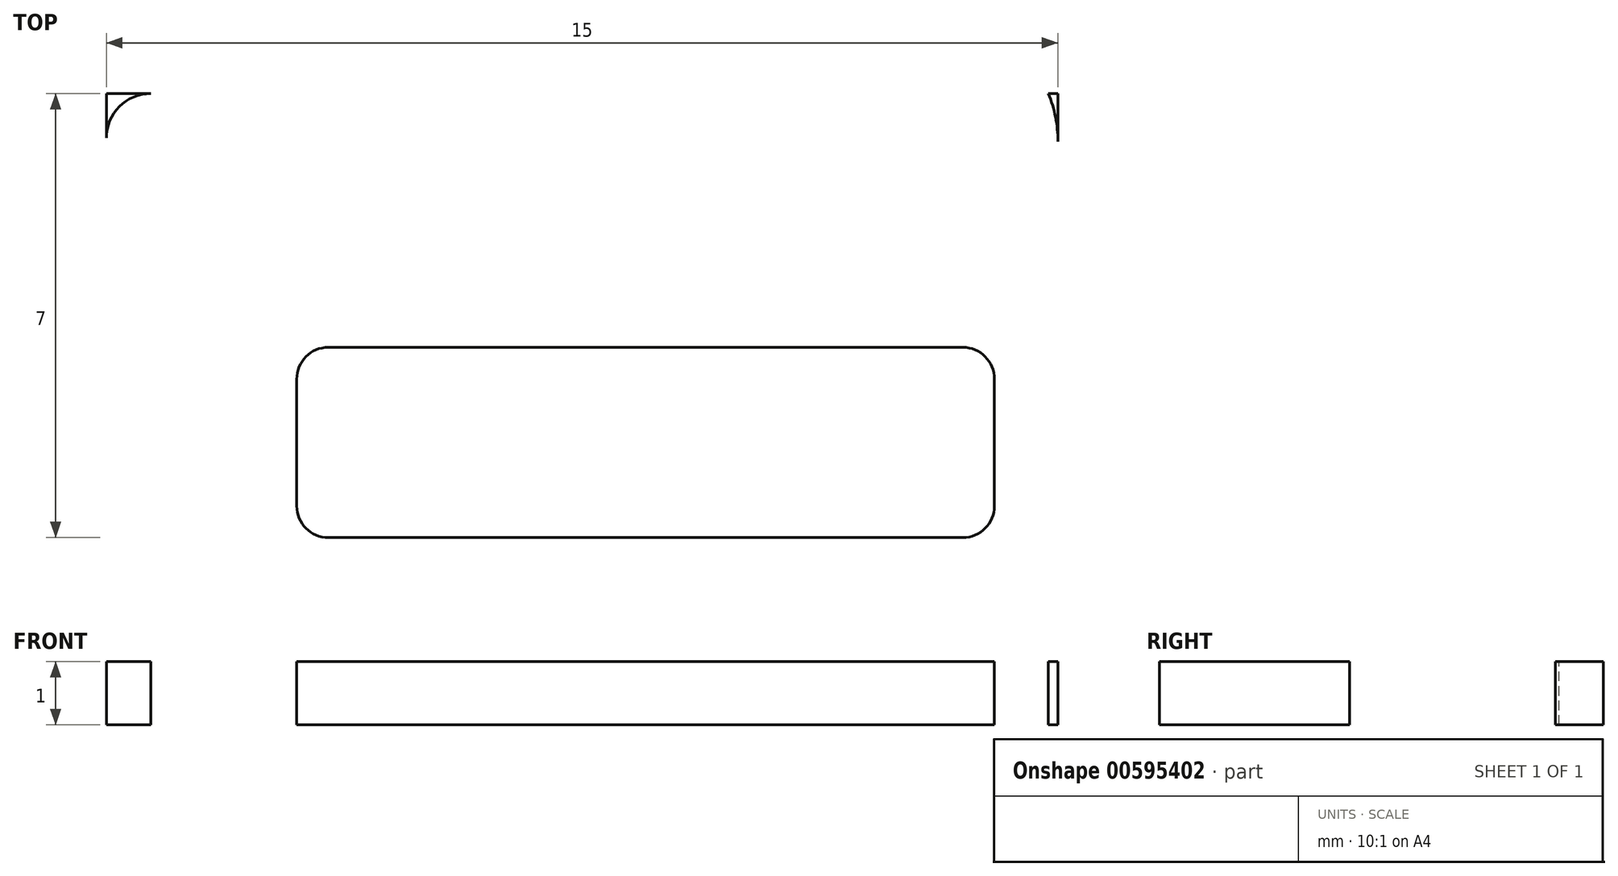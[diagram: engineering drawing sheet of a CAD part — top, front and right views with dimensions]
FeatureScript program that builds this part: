
annotation { "Feature Type Name" : "Feature", "Feature Type Description" : "" }
export const myFeature = defineFeature(function(context is Context, id is Id, definition is map)
    precondition{}
    {
        {
            var Q0;
            Q0=qCreatedBy(makeId("Top.planeOp"),FACE);
            var sketch = newSketch(context, id + "F0", { "sketchPlane" : qUnion([Q0])});
            skLineSegment(sketch, "E0.bottom", {"start": v(7.5, 4.95) * mm, "end": v(-7.5, 4.95) * mm});
            skLineSegment(sketch, "E0.top", {"start": v(7.5, -4.95) * mm, "end": v(-7.5, -4.95) * mm});
            skLineSegment(sketch, "E0.left", {"start": v(7.5, 4.95) * mm, "end": v(7.5, -4.95) * mm});
            skLineSegment(sketch, "E0.right", {"start": v(-7.5, 4.95) * mm, "end": v(-7.5, -4.95) * mm});
            skPoint(sketch, "E0.middle", {"position": v(0, 0) * mm});
            skSolve(sketch);
        }
        {
            var Q0;
            Q0 = qSketchRegion(id + "F0", true);
            extrude(context, id + "F1", {"entities" : qUnion([Q0]), "depth" : 1 * mm, "offsetDistance" : 25 * mm});
        }
        {
            var Q0;
            Q0=makeQuery(id+"F1.opExtrude","CAP_FACE",FACE,{"disambiguationData":[OSD([sQuery(id+"F0.wireOp",EDGE,"E0.bottom"),sQuery(id+"F0.wireOp",EDGE,"E0.top"),sQuery(id+"F0.wireOp",EDGE,"E0.left"),sQuery(id+"F0.wireOp",EDGE,"E0.right")])],"isStart":false});
            var sketch = newSketch(context, id + "F2", { "sketchPlane" : qUnion([Q0])});
            skLineSegment(sketch, "E1", {"start": v(-13.1, -4.82) * mm, "end": v(-1.33, -6.84) * mm});
            skLineSegment(sketch, "E2", {"start": v(-1.67, -6.8) * mm, "end": v(5.5, -6.8) * mm});
            skLineSegment(sketch, "E3", {"start": v(7.5, -4.8) * mm, "end": v(7.5, 4.2) * mm});
            skLineSegment(sketch, "E4", {"start": v(5.5, 6.2) * mm, "end": v(-1.61, 6.2) * mm});
            skLineSegment(sketch, "E5", {"start": v(145.29, 22.9) * mm, "end": v(-1.39, 6.2) * mm});
            skLineSegment(sketch, "E6", {"start": v(-4, 0.95) * mm, "end": v(6, 0.95) * mm});
            skLineSegment(sketch, "E7", {"start": v(6.5, 0.45) * mm, "end": v(6.5, -1.55) * mm});
            skLineSegment(sketch, "E8", {"start": v(6, -2.05) * mm, "end": v(-4, -2.05) * mm});
            skLineSegment(sketch, "E9", {"start": v(-4.5, -1.55) * mm, "end": v(-4.5, 0.45) * mm});
            skLineSegment(sketch, "E10", {"start": v(-4.5, -6.55) * mm, "end": v(-4.5, -8.55) * mm});
            skLineSegment(sketch, "E11", {"start": v(-4, -9.05) * mm, "end": v(6, -9.05) * mm});
            skLineSegment(sketch, "E12", {"start": v(6.5, -8.55) * mm, "end": v(6.5, -6.55) * mm});
            skLineSegment(sketch, "E13", {"start": v(6, -6.05) * mm, "end": v(-4, -6.05) * mm});
            skLineSegment(sketch, "E14", {"start": v(-4.5, -13.55) * mm, "end": v(-4.5, -15.55) * mm});
            skLineSegment(sketch, "E15", {"start": v(-4, -16.05) * mm, "end": v(6, -16.05) * mm});
            skLineSegment(sketch, "E16", {"start": v(6.5, -15.55) * mm, "end": v(6.5, -13.55) * mm});
            skLineSegment(sketch, "E17", {"start": v(6, -13.05) * mm, "end": v(-4, -13.05) * mm});
            skPoint(sketch, "E18.visualSharp", {"position": v(7.5, -6.8) * mm});
            skArc(sketch, "E18.filletArc", {"start": v(5.5, -6.8) * mm, "mid": v(6.91, -6.22) * mm, "end": v(7.5, -4.8) * mm});
            skPoint(sketch, "E19.visualSharp", {"position": v(7.5, 6.2) * mm});
            skArc(sketch, "E19.filletArc", {"start": v(7.5, 4.2) * mm, "mid": v(6.91, 5.6) * mm, "end": v(5.5, 6.2) * mm});
            skPoint(sketch, "E20.visualSharp", {"position": v(-1.5, 6.2) * mm});
            skArc(sketch, "E20.filletArc", {"start": v(-1.39, 6.2) * mm, "mid": v(-1.73, 10.2) * mm, "end": v(-1.61, 6.2) * mm});
            skPoint(sketch, "E21.visualSharp", {"position": v(-1.5, -6.8) * mm});
            skArc(sketch, "E21.filletArc", {"start": v(-1.67, -6.8) * mm, "mid": v(-1.84, -10.8) * mm, "end": v(-1.33, -6.84) * mm});
            skPoint(sketch, "E22.visualSharp", {"position": v(6.5, 0.95) * mm});
            skArc(sketch, "E22.filletArc", {"start": v(6.5, 0.45) * mm, "mid": v(6.35, 0.8) * mm, "end": v(6, 0.95) * mm});
            skPoint(sketch, "E23.visualSharp", {"position": v(6.5, -2.05) * mm});
            skArc(sketch, "E23.filletArc", {"start": v(6, -2.05) * mm, "mid": v(6.35, -1.9) * mm, "end": v(6.5, -1.55) * mm});
            skPoint(sketch, "E24.visualSharp", {"position": v(-4.5, 0.95) * mm});
            skArc(sketch, "E24.filletArc", {"start": v(-4, 0.95) * mm, "mid": v(-4.35, 0.8) * mm, "end": v(-4.5, 0.45) * mm});
            skPoint(sketch, "E25.visualSharp", {"position": v(-4.5, -2.05) * mm});
            skArc(sketch, "E25.filletArc", {"start": v(-4.5, -1.55) * mm, "mid": v(-4.35, -1.9) * mm, "end": v(-4, -2.05) * mm});
            skPoint(sketch, "E26.visualSharp", {"position": v(-4.5, -6.05) * mm});
            skArc(sketch, "E26.filletArc", {"start": v(-4, -6.05) * mm, "mid": v(-4.35, -6.2) * mm, "end": v(-4.5, -6.55) * mm});
            skPoint(sketch, "E27.visualSharp", {"position": v(-4.5, -9.05) * mm});
            skArc(sketch, "E27.filletArc", {"start": v(-4.5, -8.55) * mm, "mid": v(-4.35, -8.9) * mm, "end": v(-4, -9.05) * mm});
            skPoint(sketch, "E28.visualSharp", {"position": v(6.5, -6.05) * mm});
            skArc(sketch, "E28.filletArc", {"start": v(6.5, -6.55) * mm, "mid": v(6.35, -6.2) * mm, "end": v(6, -6.05) * mm});
            skPoint(sketch, "E29.visualSharp", {"position": v(6.5, -9.05) * mm});
            skArc(sketch, "E29.filletArc", {"start": v(6, -9.05) * mm, "mid": v(6.35, -8.9) * mm, "end": v(6.5, -8.55) * mm});
            skPoint(sketch, "E30.visualSharp", {"position": v(6.5, -13.05) * mm});
            skArc(sketch, "E30.filletArc", {"start": v(6.5, -13.55) * mm, "mid": v(6.35, -13.2) * mm, "end": v(6, -13.05) * mm});
            skPoint(sketch, "E31.visualSharp", {"position": v(-4.5, -13.05) * mm});
            skArc(sketch, "E31.filletArc", {"start": v(-4, -13.05) * mm, "mid": v(-4.35, -13.2) * mm, "end": v(-4.5, -13.55) * mm});
            skPoint(sketch, "E32.visualSharp", {"position": v(-4.5, -16.05) * mm});
            skArc(sketch, "E32.filletArc", {"start": v(-4.5, -15.55) * mm, "mid": v(-4.35, -15.9) * mm, "end": v(-4, -16.05) * mm});
            skPoint(sketch, "E33.visualSharp", {"position": v(6.5, -16.05) * mm});
            skArc(sketch, "E33.filletArc", {"start": v(6, -16.05) * mm, "mid": v(6.35, -15.9) * mm, "end": v(6.5, -15.55) * mm});
            skLineSegment(sketch, "E34", {"start": v(-6.8, 4.95) * mm, "end": v(-24.55, 4.95) * mm});
            skLineSegment(sketch, "E35", {"start": v(-7.5, 11.64) * mm, "end": v(-7.5, 4.25) * mm});
            skPoint(sketch, "E36.visualSharp", {"position": v(-7.5, 4.95) * mm});
            skArc(sketch, "E36.filletArc", {"start": v(-6.8, 4.95) * mm, "mid": v(-7.3, 4.74) * mm, "end": v(-7.5, 4.25) * mm});
            skLineSegment(sketch, "E37", {"start": v(-2.68, 4.95) * mm, "end": v(146.3, 4.95) * mm});
            skPoint(sketch, "E38.visualSharp", {"position": v(-12.43, 4.95) * mm});
            skArc(sketch, "E38.filletArc", {"start": v(145.29, 22.9) * mm, "mid": v(137.32, 13.44) * mm, "end": v(146.3, 4.95) * mm});
            skLineSegment(sketch, "E39", {"start": v(3.64, -4.95) * mm, "end": v(-11.58, -4.95) * mm});
            skPoint(sketch, "E40.visualSharp", {"position": v(-12.34, -4.95) * mm});
            skArc(sketch, "E40.filletArc", {"start": v(-11.58, -4.95) * mm, "mid": v(-10.81, 13.02) * mm, "end": v(-13.1, -4.82) * mm});
            skLineSegment(sketch, "E41", {"start": v(-7.5, 4.95) * mm, "end": v(-15.38, 4.95) * mm});
            skSolve(sketch);
        }
        {
            var Q0;
            Q0 = qSketchRegion(id + "F2", true);
            var Q1;
            {var subQ0=sQuery(id+"F2.wireOp",EDGE,"E4");Q1=makeQuery(id+"F2.imprint","IMPRINT",FACE,{"disambiguationData":[TD([[makeQuery(id+"F2.imprint","IMPRINT",EDGE,{"derivedFrom":subQ0}),-1.0]])]});}
            var Q2;
            {var subQ0=sQuery(id+"F2.wireOp",EDGE,"E1");Q2=makeQuery(id+"F2.imprint","IMPRINT",FACE,{"disambiguationData":[TD([[makeQuery(id+"F2.imprint","IMPRINT",EDGE,{"derivedFrom":subQ0}),-1.0]])]});}
            extrude(context, id + "F3", {"entities" : qUnion([Q0, Q1, Q2]), "operationType" : NewBodyOperationType.REMOVE, "oppositeDirection" : true, "depth" : 25 * mm, "offsetDistance" : 25 * mm});
        }
    });
